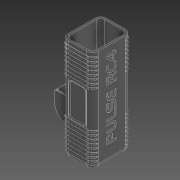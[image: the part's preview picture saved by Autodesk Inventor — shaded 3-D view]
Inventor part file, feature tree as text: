
AUTODESK INVENTOR PART (.ipt)
format: ipt  version: 2021 (Build 250183000, 183)  size: 2,327,552 bytes
history: native  units: mm
features: extrude x36, sketch x34, projected_geometry x19, fillet x18, plane x8, mirror x7, other x1
ambient origin geometry x8: Origin, YZ Plane, XZ Plane, XY Plane, X Axis, Y Axis, Z Axis, Center Point
bodies: Body1 (feature_tree)
feature tree (123):
  other  "Sólido1"
  extrude  "Extrusión1"  Depth=36.5mm
  extrude  "Extrusión2"  Depth=6.0mm
  extrude  "Extrusión3"  Depth=4.0mm
  plane  "Plano de trabajo1"
  mirror  "Simetría1"
  fillet  "Empalme1"  Radius=108.0mm
  plane  "Plano de trabajo2"
  extrude  "Extrusión4"  Depth=8.0mm
  plane  "Plano de trabajo3"
  mirror  "Simetría2"
  plane  "Plano de trabajo4"
  mirror  "Simetría3"
  plane  "Plano de trabajo5"
  mirror  "Simetría4"
  plane  "Plano de trabajo6"
  mirror  "Simetría5"
  plane  "Plano de trabajo8"
  mirror  "Simetría6"
  fillet  "Empalme2"  Radius=2.0mm
  fillet  "Empalme3"  Radius=2.0mm
  sketch  "Boceto4"  dims[d4=4.0mm d5=4.0mm d6=108.0mm d7=0.0mm]
  extrude  "Extrusión5"  Depth=2.0mm TaperAngle=0.0deg
  extrude  "Extrusión6"  Depth=6.0mm
  extrude  "Extrusión7"  Depth=11.0mm
  extrude  "Extrusión8"  [1 undecoded]
  extrude  "Extrusión9"  Depth=5.0mm
  extrude  "Extrusión10"  [1 undecoded]
  extrude  "Extrusión11"  [1 undecoded]
  extrude  "Extrusión12"  Depth=1.0mm
  extrude  "Extrusión13"  Depth=0.6mm TaperAngle=0.0deg
  extrude  "Extrusión14"  Depth=9.0mm
  extrude  "Extrusión15"  Depth=14.0mm TaperAngle=0.0deg
  extrude  "Extrusión16"  Depth=7.0mm
  fillet  "Empalme10"  Radius=1.8mm
  extrude  "Extrusión17"  Depth=2.0mm
  fillet  "Empalme13"  Radius=7.0mm
  fillet  "Empalme16"  Radius=6.0mm
  extrude  "Extrusión18"  Depth=8.0mm TaperAngle=0.0deg
  extrude  "Extrusión19"  Depth=8.0mm TaperAngle=0.0deg
  fillet  "Empalme31"  Radius=75.0mm
  fillet  "Empalme32"  Radius=75.0mm
  extrude  "Extrusión20"  Depth=11.273282mm
  extrude  "Extrusión21"  Depth=9.0mm
  extrude  "Extrusión22"  Depth=10.0mm TaperAngle=0.0deg
  extrude  "Extrusión23"  Depth=4.0mm
  mirror  "Simetría8"
  extrude  "Extrusión25"  Depth=2.0mm
  extrude  "Extrusión31"  Depth=0.5mm TaperAngle=0.0deg
  extrude  "Extrusión32"  Depth=0.5mm TaperAngle=0.0deg
  extrude  "Extrusión33"  Depth=4.0mm
  fillet  "Empalme39"  Radius=12.0mm
  extrude  "Extrusión34"  Depth=1.653837mm
  extrude  "Extrusión35"  Depth=10.0mm TaperAngle=0.0deg
  extrude  "Extrusión36"  Depth=5.0mm
  extrude  "Extrusión37"  Depth=10.0mm TaperAngle=0.0deg
  fillet  "Empalme41"  Radius=16.9mm
  fillet  "Empalme42"  Radius=10.0mm
  fillet  "Empalme43"  Radius=10.0mm
  fillet  "Empalme44"  Radius=9.0mm
  fillet  "Empalme45"  [1 undecoded]
  fillet  "Empalme46"  Radius=1.55mm
  plane  "Plano de trabajo11"
  extrude  "Extrusión38"  Depth=10.0mm TaperAngle=0.0deg
  extrude  "Extrusión39"  Depth=10.0mm
  extrude  "Extrusión40"  Depth=1.0mm TaperAngle=0.0deg
  fillet  "Empalme47"  Radius=14.9mm
  extrude  "Extrusión41"  Depth=4.0mm TaperAngle=0.0deg
  fillet  "Empalme48"  Radius=2.0mm
  fillet  "Empalme49"  Radius=2.0mm
  extrude  "Extrusión42"  Depth=0.5mm
  sketch  "Boceto2"  dims[d0=27.85mm d1=36.5mm]
  sketch  "Boceto3"  dims[d2=2.0mm d3=6.0mm]
  sketch  "Boceto5"  dims[d8=2.0mm d9=0.0mm d10=8.0mm d11=2.0mm d12=2.0mm]
  sketch  "Boceto6"  dims[d13=2.0mm d14=2.0mm d15=0.0mm]
  sketch  "Boceto7"  dims[d16=20.0mm d17=6.0mm]
  sketch  "Boceto8"  dims[d18=3.2mm d19=11.0mm]
  projected_geometry  "Contorno proyectado1"
  sketch  "Boceto9"  dims[d20=5.0mm d21=-4.0mm]
  sketch  "Boceto10"  dims[d22=0.8mm d23=5.0mm]
  sketch  "Boceto11"  dims[d24=2.0mm d25=0.0mm d26=-3.0mm]
  sketch  "Boceto12"  dims[d27=-4.0mm d28=-8.0mm]
  sketch  "Boceto13"  dims[d29=-33.5mm d30=1.0mm]
  projected_geometry  "Contorno proyectado2"
  sketch  "Boceto14"  dims[d31=1.0mm d32=0.6mm d33=0.0mm]
  sketch  "Boceto18"  dims[d37=20.0mm d39=9.0mm]
  sketch  "Boceto19"  dims[d40=24.0mm d41=14.0mm d42=0.0mm]
  projected_geometry  "Contorno proyectado7"
  sketch  "Boceto20"  dims[d43=8.0mm d44=0.0mm d45=7.0mm d46=1.8mm]
  sketch  "Boceto21"  dims[d47=15.0mm d48=0.0mm d49=2.0mm d50=7.0mm d51=0.0mm d53=6.0mm d54=0.0mm]
  sketch  "Boceto22"  dims[d56=14.0mm d57=0.0mm d58=8.0mm d59=0.0mm]
  sketch  "Boceto24"  dims[d60=8.0mm d61=0.0mm d63=8.0mm d64=0.0mm d65=75.0mm d66=75.0mm]
  projected_geometry  "Contorno proyectado9"
  sketch  "Boceto25"  dims[d67=16.5mm d68=11.273282mm]
  sketch  "Boceto26"  dims[d70=5.0mm d72=9.0mm]
  projected_geometry  "Contorno proyectado10"
  projected_geometry  "Contorno proyectado11"
  projected_geometry  "Contorno proyectado12"
  projected_geometry  "Contorno proyectado13"
  sketch  "Boceto30"  dims[d73=9.0mm d75=10.0mm d76=0.0mm]
  projected_geometry  "Contorno proyectado16"
  sketch  "Boceto35"  dims[d78=6.0mm d79=4.0mm]
  projected_geometry  "Contorno proyectado21"
  sketch  "Boceto36"  dims[d80=6.0mm d81=2.0mm]
  projected_geometry  "Contorno proyectado22"
  projected_geometry  "Contorno proyectado23"
  sketch  "Boceto37"  dims[d82=2.0mm d83=0.5mm d84=0.0mm]
  projected_geometry  "Contorno proyectado24"
  sketch  "Boceto38"  dims[d85=2.0mm d88=0.5mm d89=0.0mm]
  projected_geometry  "Contorno proyectado25"
  sketch  "Boceto39"  dims[d90=1.5mm d93=4.0mm d96=12.0mm]
  projected_geometry  "Contorno proyectado26"
  sketch  "Boceto40"  dims[d97=1.5mm d98=1.653837mm]
  sketch  "Boceto41"  dims[d99=10.0mm d100=0.0mm d101=10.0mm d102=0.0mm]
  sketch  "Boceto42"  dims[d115=1.0mm d116=5.0mm]
  sketch  "Boceto43"  dims[d117=1.0mm d118=10.0mm d119=0.0mm d122=16.9mm d123=10.0mm d124=0.0mm d125=10.0mm d126=0.0mm d127=9.0mm d128=0.0mm d133=0.0mm d134=0.0mm d149=1.55mm]
  sketch  "Boceto44"  dims[d150=10.0mm d151=0.0mm d152=10.0mm d153=0.0mm]
  projected_geometry  "Contorno proyectado29"
  projected_geometry  "Contorno proyectado30"
  projected_geometry  "Contorno proyectado31"
  sketch  "Boceto45"  dims[d154=10.0mm d155=0.0mm d156=13.0mm]
  sketch  "Boceto46"  dims[d157=7.5mm d158=0.0mm d160=1.0mm d161=0.0mm d162=14.9mm d163=0.0mm d164=4.0mm d165=0.0mm d166=2.0mm d167=2.0mm d168=0.5mm d169=1.5mm d170=2.0mm d171=2.0mm d172=-13.0mm d173=6.2mm d174=4.0mm d175=0.0mm d176=4.0mm d177=0.0mm d178=4.0mm d179=0.0mm d180=2.0mm d181=3.0mm d182=2.0mm d183=0.0mm d184=2.0mm d185=1.0mm d186=26.0mm d187=0.0mm d74=0.5mm d77=0.872665mm d159=0.5mm]
  projected_geometry  "Contorno proyectado32"
note: 4 required parameter values undecoded (feature->parameter linkage not recoverable at this tier; creation-order binding heuristic only, values carry confidence <= 0.55)
